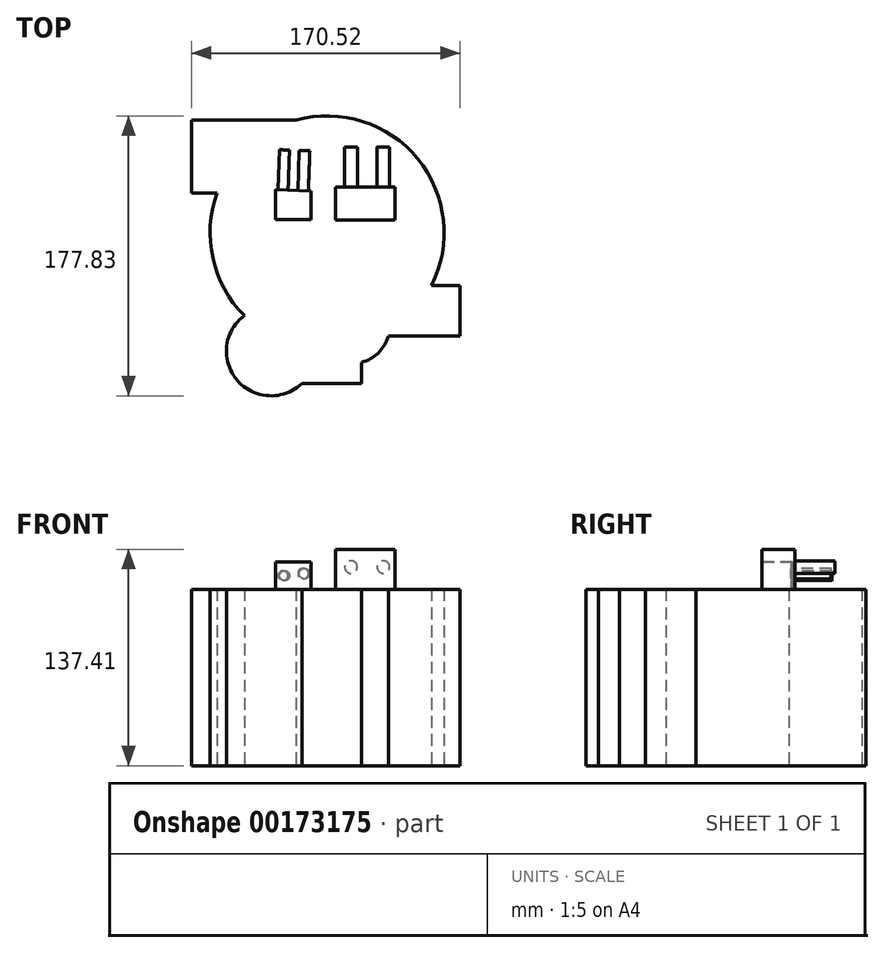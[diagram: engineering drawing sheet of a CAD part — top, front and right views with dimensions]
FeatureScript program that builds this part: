
annotation { "Feature Type Name" : "Feature", "Feature Type Description" : "" }
export const myFeature = defineFeature(function(context is Context, id is Id, definition is map)
    precondition{}
    {
        {
            var Q0;
            Q0=qCreatedBy(makeId("Top.planeOp"),FACE);
            var sketch = newSketch(context, id + "F0", { "sketchPlane" : qUnion([Q0])});
            skArc(sketch, "E0", {"start": v(-77.45, 1.03) * mm, "mid": v(-82.09, -39.96) * mm, "end": v(-40.89, -42.01) * mm});
            skLineSegment(sketch, "E1.top", {"start": v(-40.89, -42.01) * mm, "end": v(-3.13, -42.01) * mm});
            skArc(sketch, "E2", {"start": v(-3.13, -28.74) * mm, "mid": v(7.65, -22.62) * mm, "end": v(14.12, -12.05) * mm});
            skLineSegment(sketch, "E3.bottom", {"start": v(41.48, 20.08) * mm, "end": v(59.54, 20.08) * mm});
            skLineSegment(sketch, "E3.top", {"start": v(14.12, -12.05) * mm, "end": v(59.54, -12.05) * mm});
            skLineSegment(sketch, "E3.right", {"start": v(59.54, 20.08) * mm, "end": v(59.54, -12.05) * mm});
            skArc(sketch, "E4", {"start": v(41.48, 20.08) * mm, "mid": v(32.63, 100.66) * mm, "end": v(-44.63, 125.22) * mm});
            skLineSegment(sketch, "E5.trimOffspring", {"start": v(-3.13, -28.74) * mm, "end": v(-3.13, -42.01) * mm});
            skPoint(sketch, "E6.orphan", {"position": v(-60.52, -49.06) * mm});
            skLineSegment(sketch, "E7.bottom", {"start": v(-110.98, 125.22) * mm, "end": v(-44.63, 125.22) * mm});
            skLineSegment(sketch, "E7.top", {"start": v(-110.98, 79) * mm, "end": v(-94.71, 79) * mm});
            skLineSegment(sketch, "E7.left", {"start": v(-110.98, 125.22) * mm, "end": v(-110.98, 79) * mm});
            skArc(sketch, "E8.trimOffspring", {"start": v(-94.71, 79) * mm, "mid": v(-97.44, 37.5) * mm, "end": v(-77.45, 1.03) * mm});
            skSolve(sketch);
        }
        {
            var Q0;
            Q0=makeQuery(id+"F0.imprint","IMPRINT",FACE,{"disambiguationData":[TD([[makeQuery(id+"F0.imprint","IMPRINT",EDGE,{"derivedFrom":sQuery(id+"F0.wireOp",EDGE,"E0")}),1.0]])]});
            extrude(context, id + "F1", {"entities" : qUnion([Q0]), "depth" : 112.01 * mm});
        }
        {
            var Q0;
            Q0=makeQuery(id+"F1.opExtrude","CAP_FACE",FACE,{"disambiguationData":[OSD([sQuery(id+"F0.wireOp",EDGE,"E0"),sQuery(id+"F0.wireOp",EDGE,"E1.top"),sQuery(id+"F0.wireOp",EDGE,"E2"),sQuery(id+"F0.wireOp",EDGE,"E3.bottom"),sQuery(id+"F0.wireOp",EDGE,"E3.top"),sQuery(id+"F0.wireOp",EDGE,"E3.right"),sQuery(id+"F0.wireOp",EDGE,"E4"),sQuery(id+"F0.wireOp",EDGE,"E5.trimOffspring"),sQuery(id+"F0.wireOp",EDGE,"E7.bottom"),sQuery(id+"F0.wireOp",EDGE,"E7.top"),sQuery(id+"F0.wireOp",EDGE,"E7.left"),sQuery(id+"F0.wireOp",EDGE,"E8.trimOffspring")])],"isStart":false});
            var sketch = newSketch(context, id + "F2", { "sketchPlane" : qUnion([Q0])});
            skLineSegment(sketch, "E9", {"start": v(-57.52, 81.06) * mm, "end": v(-57.52, 62.17) * mm});
            skLineSegment(sketch, "E10", {"start": v(-57.52, 62.17) * mm, "end": v(-34.96, 62.17) * mm});
            skLineSegment(sketch, "E11", {"start": v(-34.96, 62.17) * mm, "end": v(-34.96, 80.27) * mm});
            skLineSegment(sketch, "E12", {"start": v(-34.96, 80.27) * mm, "end": v(-57.52, 81.06) * mm});
            skSolve(sketch);
        }
        {
            var Q0;
            Q0=makeQuery(id+"F2.imprint","IMPRINT",FACE,{"disambiguationData":[TD([[makeQuery(id+"F2.imprint","IMPRINT",EDGE,{"derivedFrom":sQuery(id+"F2.wireOp",EDGE,"E9")}),1.0]])]});
            extrude(context, id + "F3", {"entities" : qUnion([Q0]), "operationType" : NewBodyOperationType.ADD, "depth" : 17.27 * mm});
        }
        {
            var Q0;
            Q0=makeQuery(id+"F3.opExtrude","SWEPT_FACE",FACE,{"disambiguationData":[OSD([sQuery(id+"F2.wireOp",EDGE,"E12")])]});
            var sketch = newSketch(context, id + "F4", { "sketchPlane" : qUnion([Q0])});
            skCircle(sketch, "E13", {"center": v(42.88, 122.01) * mm, "radius": 3.36 * mm});
            skCircle(sketch, "E14", {"center": v(55.57, 122.01) * mm, "radius": 3.18 * mm});
            skSolve(sketch);
        }
        {
            var Q0;
            Q0=makeQuery(id+"F4.imprint","IMPRINT",FACE,{"disambiguationData":[TD([[makeQuery(id+"F4.imprint","IMPRINT",EDGE,{"derivedFrom":sQuery(id+"F4.wireOp",EDGE,"E13")}),1.0]])]});
            extrude(context, id + "F5", {"entities" : qUnion([Q0]), "operationType" : NewBodyOperationType.ADD, "depth" : 25.4 * mm});
        }
        {
            var Q0;
            Q0=makeQuery(id+"F3.opExtrude","SWEPT_FACE",FACE,{"disambiguationData":[OSD([sQuery(id+"F2.wireOp",EDGE,"E12")])]});
            var sketch = newSketch(context, id + "F6", { "sketchPlane" : qUnion([Q0])});
            skCircle(sketch, "E15", {"center": v(55.57, 120.65) * mm, "radius": 3.15 * mm});
            skPoint(sketch, "E15.centerSnap0", {"position": v(60.31, 120.65) * mm});
            skSolve(sketch);
        }
        {
            var Q0;
            Q0=makeQuery(id+"F6.imprint","IMPRINT",FACE,{"disambiguationData":[TD([[makeQuery(id+"F6.imprint","IMPRINT",EDGE,{"derivedFrom":sQuery(id+"F6.wireOp",EDGE,"E15")}),1.0]])]});
            extrude(context, id + "F7", {"entities" : qUnion([Q0]), "operationType" : NewBodyOperationType.ADD, "depth" : 25.4 * mm});
        }
        {
            var Q0;
            Q0=makeQuery(id+"F1.opExtrude","CAP_FACE",FACE,{"disambiguationData":[OSD([sQuery(id+"F0.wireOp",EDGE,"E0"),sQuery(id+"F0.wireOp",EDGE,"E1.top"),sQuery(id+"F0.wireOp",EDGE,"E2"),sQuery(id+"F0.wireOp",EDGE,"E3.bottom"),sQuery(id+"F0.wireOp",EDGE,"E3.top"),sQuery(id+"F0.wireOp",EDGE,"E3.right"),sQuery(id+"F0.wireOp",EDGE,"E4"),sQuery(id+"F0.wireOp",EDGE,"E5.trimOffspring"),sQuery(id+"F0.wireOp",EDGE,"E7.bottom"),sQuery(id+"F0.wireOp",EDGE,"E7.top"),sQuery(id+"F0.wireOp",EDGE,"E7.left"),sQuery(id+"F0.wireOp",EDGE,"E8.trimOffspring")])],"isStart":false});
            var sketch = newSketch(context, id + "F8", { "sketchPlane" : qUnion([Q0])});
            skLineSegment(sketch, "E16.bottom", {"start": v(-19.64, 61.7) * mm, "end": v(18.4, 61.7) * mm});
            skLineSegment(sketch, "E16.top", {"start": v(-19.64, 82.74) * mm, "end": v(18.4, 82.74) * mm});
            skLineSegment(sketch, "E16.left", {"start": v(-19.64, 61.7) * mm, "end": v(-19.64, 82.74) * mm});
            skLineSegment(sketch, "E16.right", {"start": v(18.4, 61.7) * mm, "end": v(18.4, 82.74) * mm});
            skSolve(sketch);
        }
        {
            var Q0;
            Q0=makeQuery(id+"F8.imprint","IMPRINT",FACE,{"disambiguationData":[TD([[makeQuery(id+"F8.imprint","IMPRINT",EDGE,{"derivedFrom":sQuery(id+"F8.wireOp",EDGE,"E16.bottom")}),1.0]])]});
            extrude(context, id + "F9", {"entities" : qUnion([Q0]), "operationType" : NewBodyOperationType.ADD, "depth" : 25.4 * mm});
        }
        {
            var Q0;
            Q0=makeQuery(id+"F9.opExtrude","CAP_FACE",FACE,{"disambiguationData":[OSD([sQuery(id+"F8.wireOp",EDGE,"E16.bottom"),sQuery(id+"F8.wireOp",EDGE,"E16.top"),sQuery(id+"F8.wireOp",EDGE,"E16.left"),sQuery(id+"F8.wireOp",EDGE,"E16.right")])],"isStart":false});
            extrude(context, id + "F10", {"entities" : qUnion([Q0]), "operationType" : NewBodyOperationType.ADD, "oppositeDirection" : true, "depth" : 8.38 * mm});
        }
        {
            var Q0;
            Q0=makeQuery(id+"F9.opExtrude","CAP_FACE",FACE,{"disambiguationData":[OSD([sQuery(id+"F8.wireOp",EDGE,"E16.bottom"),sQuery(id+"F8.wireOp",EDGE,"E16.top"),sQuery(id+"F8.wireOp",EDGE,"E16.left"),sQuery(id+"F8.wireOp",EDGE,"E16.right")])],"isStart":false});
            extrude(context, id + "F11", {"entities" : qUnion([Q0]), "operationType" : NewBodyOperationType.ADD, "oppositeDirection" : true, "depth" : 10.4 * mm});
        }
        {
            var Q0;
            Q0=makeQuery(id+"F9.opExtrude","CAP_FACE",FACE,{"disambiguationData":[OSD([sQuery(id+"F8.wireOp",EDGE,"E16.bottom"),sQuery(id+"F8.wireOp",EDGE,"E16.top"),sQuery(id+"F8.wireOp",EDGE,"E16.left"),sQuery(id+"F8.wireOp",EDGE,"E16.right")])],"isStart":false});
            extrude(context, id + "F12", {"entities" : qUnion([Q0]), "operationType" : NewBodyOperationType.ADD, "oppositeDirection" : true, "depth" : 9.65 * mm});
        }
        {
            var Q0;
            Q0=makeQuery(id+"F9.opExtrude","CAP_FACE",FACE,{"disambiguationData":[OSD([sQuery(id+"F8.wireOp",EDGE,"E16.bottom"),sQuery(id+"F8.wireOp",EDGE,"E16.top"),sQuery(id+"F8.wireOp",EDGE,"E16.left"),sQuery(id+"F8.wireOp",EDGE,"E16.right")])],"isStart":false});
            extrude(context, id + "F13", {"entities" : qUnion([Q0]), "operationType" : NewBodyOperationType.ADD, "oppositeDirection" : true, "depth" : 11.68 * mm});
        }
        {
            var Q0;
            Q0=makeQuery(id+"F9.opExtrude","SWEPT_FACE",FACE,{"disambiguationData":[OSD([sQuery(id+"F8.wireOp",EDGE,"E16.top")])]});
            var sketch = newSketch(context, id + "F14", { "sketchPlane" : qUnion([Q0])});
            skCircle(sketch, "E17", {"center": v(-10.84, 126.15) * mm, "radius": 3.98 * mm});
            skCircle(sketch, "E18", {"center": v(9.68, 126.15) * mm, "radius": 4 * mm});
            skSolve(sketch);
        }
        {
            var Q0;
            Q0=makeQuery(id+"F14.imprint","IMPRINT",FACE,{"disambiguationData":[TD([[makeQuery(id+"F14.imprint","IMPRINT",EDGE,{"derivedFrom":sQuery(id+"F14.wireOp",EDGE,"E17")}),1.0]])]});
            var Q1;
            Q1=makeQuery(id+"F14.imprint","IMPRINT",FACE,{"disambiguationData":[TD([[makeQuery(id+"F14.imprint","IMPRINT",EDGE,{"derivedFrom":sQuery(id+"F14.wireOp",EDGE,"E18")}),1.0]])]});
            extrude(context, id + "F15", {"entities" : qUnion([Q0, Q1]), "operationType" : NewBodyOperationType.ADD, "depth" : 25.4 * mm});
        }
    });
